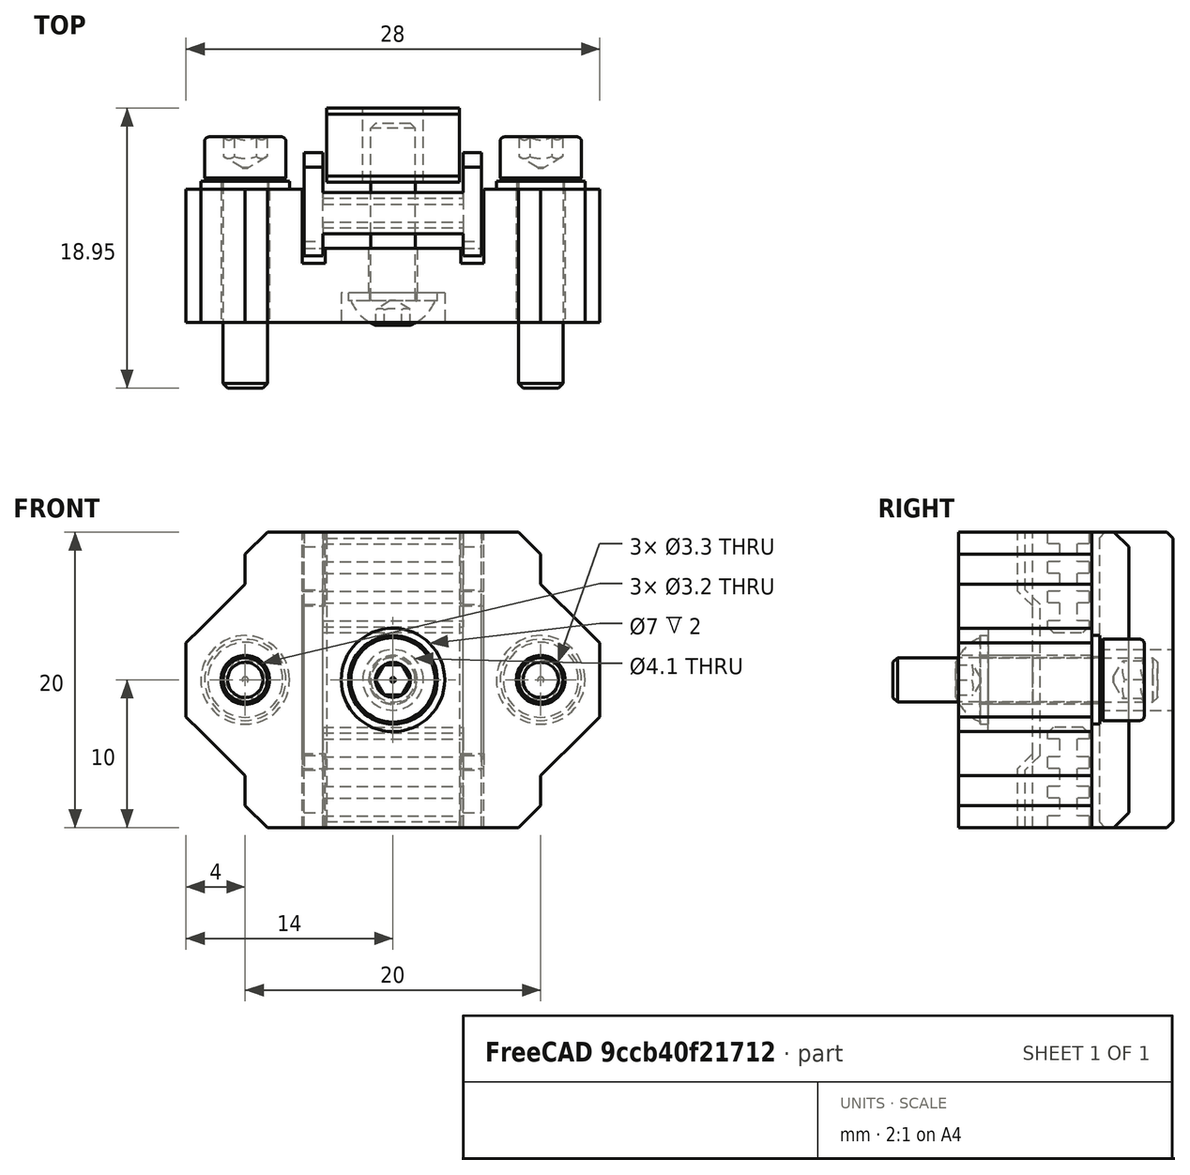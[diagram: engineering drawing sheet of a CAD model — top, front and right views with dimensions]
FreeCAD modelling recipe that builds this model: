
FCSTD DOCUMENT  (FreeCAD 0.19R24291 (Git))
Label: z-belt-mounter-assembly
License: Other
LicenseURL: GPL3
objects: Part::FeaturePython×6, Part::Feature×3, App::Part×1
note: 9 computed .brp shape members not serialized (recipe doc carries the construction recipe); baked Part::Feature solids carry a one-line shape summary decoded from their .brp

FEATURE [Part::Feature] Cut002001001  label="belt-clamp-nut001"
  Placement = pos=(0,-2,0) rot=(0,0,1;0rad)
  shape: bbox 9 x 5 x 20 mm, 11 faces (baked)
FEATURE [Part::Feature] Chamfer004013007011015006002001  label="belt-connector-rf001"
  shape: bbox 28 x 9 x 20 mm, 47 faces (baked)
FEATURE [Part::FeaturePython] Washer  label="M3-Washer"  # Fasteners workbench fastener (typed FeaturePython)
  Placement = pos=(12.5,40.5,18.5) rot=(-1,0,0;1.5708rad)
  baseObject = -> Chamfer004013007011015006002001 [Edge96]
  diameter = 4
  invert = true
  matchOuter = true
  offset = 0
  type = 5
FEATURE [Part::FeaturePython] Washer001  label="M3-Washer001"  # Fasteners workbench fastener (typed FeaturePython)
  Placement = pos=(-7.5,40.5,18.5) rot=(-1,0,0;1.5708rad)
  baseObject = -> Chamfer004013007011015006002001 [Edge15]
  diameter = 4
  invert = true
  matchOuter = true
  offset = 0
  type = 5
FEATURE [Part::FeaturePython] Screw  label="M3x14-Screw"  # Fasteners workbench fastener (typed FeaturePython)
  Placement = pos=(12.5,41.05,18.5) rot=(-1,0,0;1.5708rad)
  baseObject = -> Washer [Edge1]
  diameter = 4
  invert = false
  length = 5
  lengthCustom = 14
  matchOuter = true
  offset = 0
  thread = false
  type = 33
FEATURE [Part::FeaturePython] Screw001  label="M3x14-Screw001"  # Fasteners workbench fastener (typed FeaturePython)
  Placement = pos=(-7.5,41.05,18.5) rot=(-1,0,0;1.5708rad)
  baseObject = -> Washer001 [Edge1]
  diameter = 4
  invert = false
  length = 5
  lengthCustom = 14
  matchOuter = true
  offset = 0
  thread = false
  type = 33
FEATURE [Part::FeaturePython] Washer002  label="M3-Washer002"  # Fasteners workbench fastener (typed FeaturePython)
  Placement = pos=(2.5,33.5,18.5) rot=(1,0,0;1.5708rad)
  baseObject = -> Chamfer004013007011015006002001 [Edge132]
  diameter = 4
  invert = false
  matchOuter = true
  offset = 0
  type = 5
FEATURE [Part::FeaturePython] Screw002  label="M3x12-Screw"  # Fasteners workbench fastener (typed FeaturePython)
  Placement = pos=(2.5,32.95,18.5) rot=(1,0,0;1.5708rad)
  baseObject = -> Washer002 [Edge1]
  diameter = 1
  invert = false
  length = 9
  lengthCustom = 12
  matchOuter = true
  offset = 0
  thread = false
  type = 39
FEATURE [Part::Feature] Cut028006004005011004003001001  label="belt-mounter-9mm002"
  Placement = pos=(0,-1,0) rot=(0,0,1;0rad)
  shape: bbox 12 x 7 x 20 mm, 80 faces (baked)
FEATURE [App::Part] Part  label="z-belt-mounter"
  Group = -> [Cut002001001,Chamfer004013007011015006002001,Washer001,Screw,Screw002,Screw001,Washer002,Washer,Cut028006004005011004003001001]
  Origin = -> Origin
